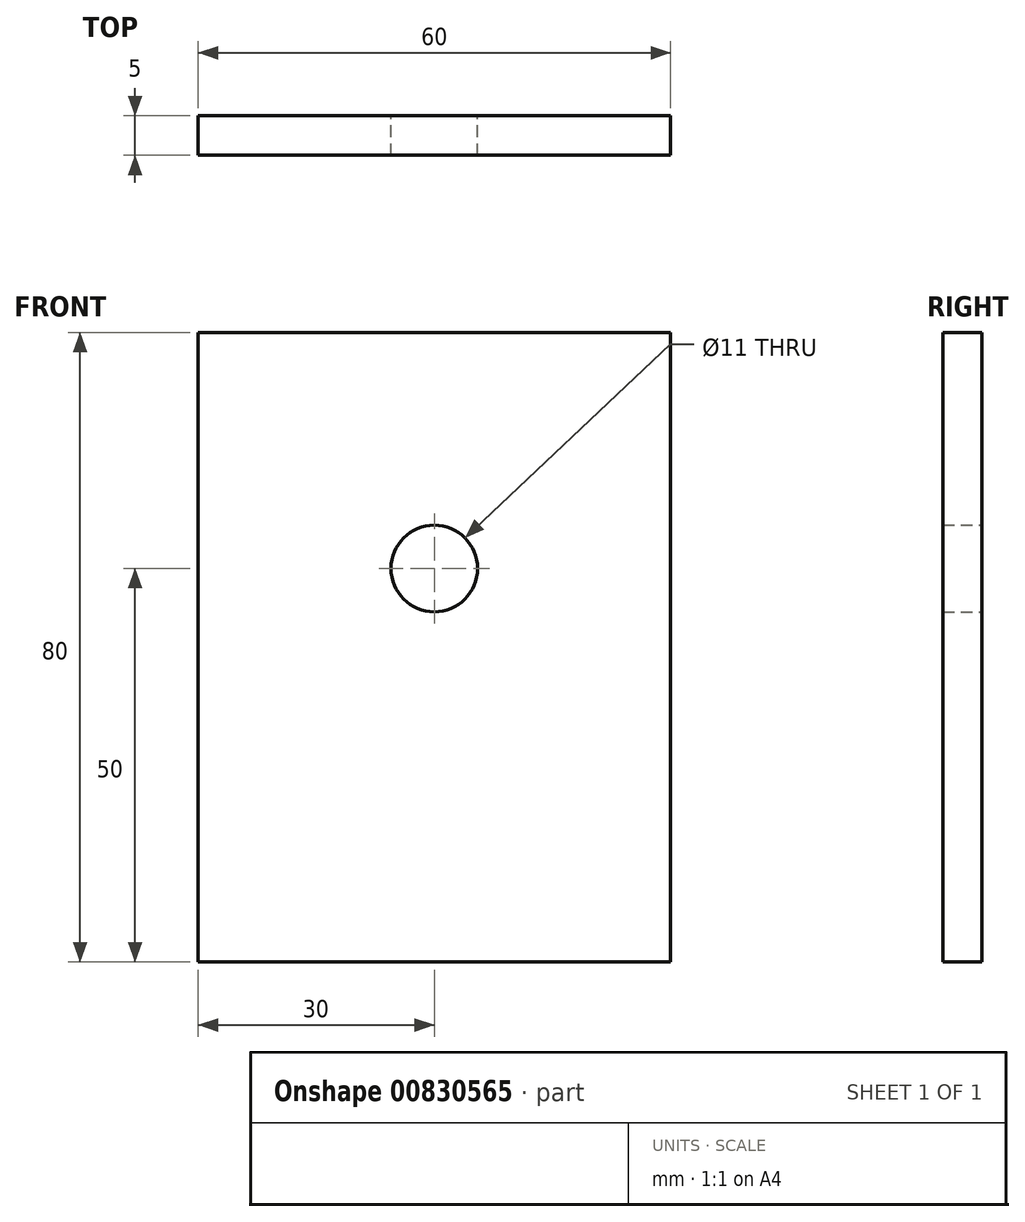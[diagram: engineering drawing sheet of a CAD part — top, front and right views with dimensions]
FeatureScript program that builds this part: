
annotation { "Feature Type Name" : "Feature", "Feature Type Description" : "" }
export const myFeature = defineFeature(function(context is Context, id is Id, definition is map)
    precondition{}
    {
        {
            var Q0;
            Q0=qCreatedBy(makeId("Front.planeOp"),FACE);
            var sketch = newSketch(context, id + "F0", { "sketchPlane" : qUnion([Q0])});
            skLineSegment(sketch, "E0.bottom", {"start": v(0, 0) * mm, "end": v(60, 0) * mm});
            skLineSegment(sketch, "E0.top", {"start": v(0, 80) * mm, "end": v(60, 80) * mm});
            skLineSegment(sketch, "E0.left", {"start": v(0, 0) * mm, "end": v(0, 80) * mm});
            skLineSegment(sketch, "E0.right", {"start": v(60, 0) * mm, "end": v(60, 80) * mm});
            skCircle(sketch, "E1", {"center": v(30, 50) * mm, "radius": 5.5 * mm});
            skSolve(sketch);
        }
        {
            var Q0;
            Q0 = qSketchRegion(id + "F0", true);
            extrude(context, id + "F1", {"entities" : qUnion([Q0]), "depth" : 5 * mm, "offsetDistance" : 25 * mm});
        }
    });
